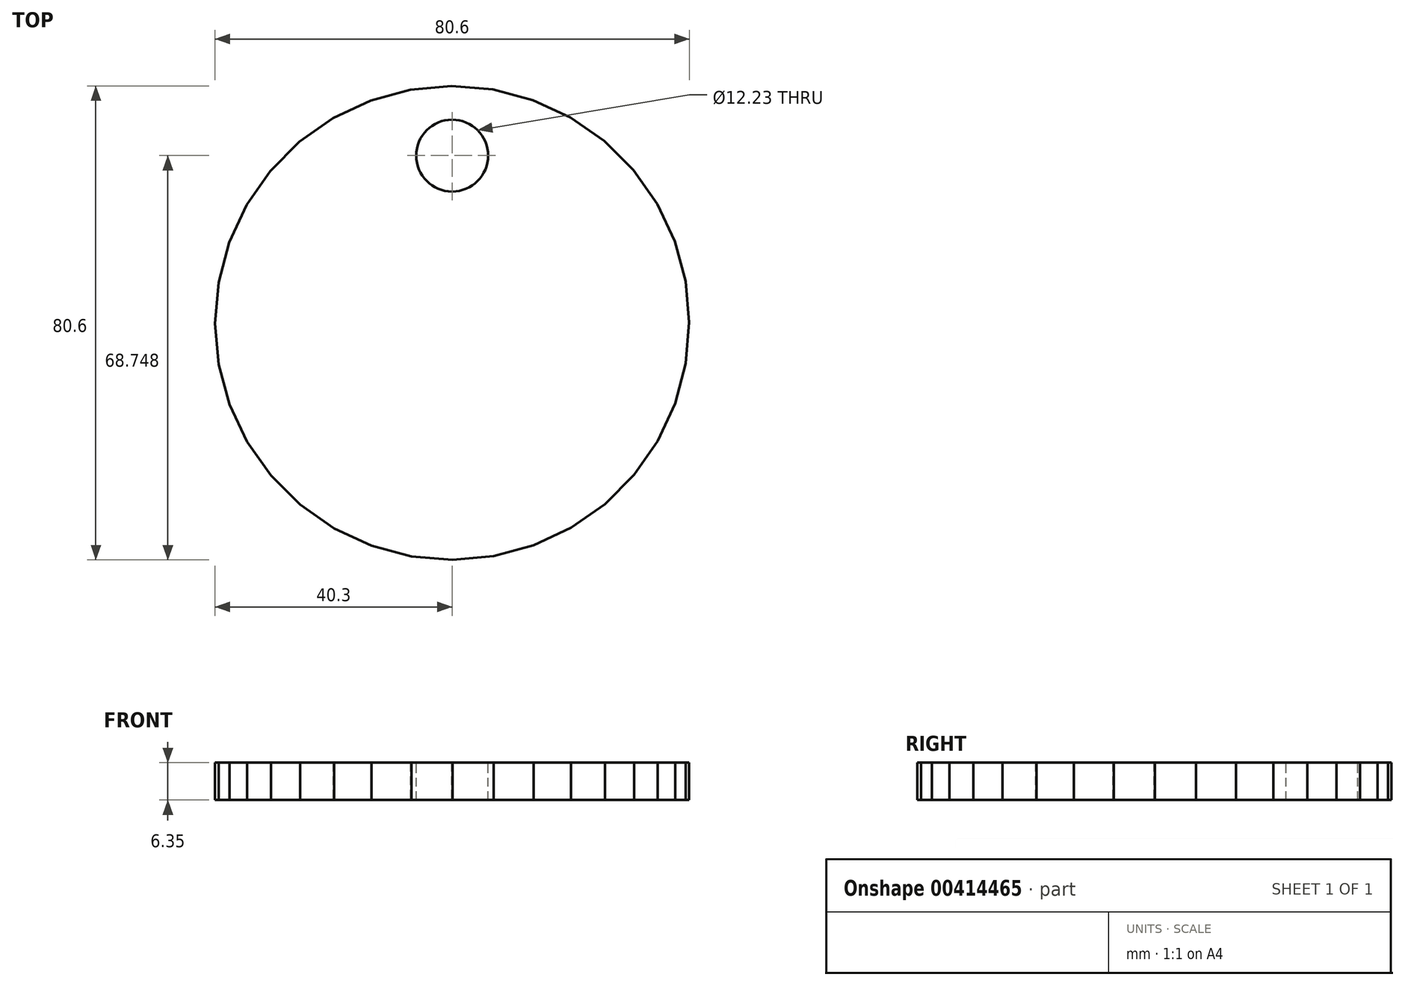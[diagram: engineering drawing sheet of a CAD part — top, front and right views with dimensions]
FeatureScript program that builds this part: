
annotation { "Feature Type Name" : "Feature", "Feature Type Description" : "" }
export const myFeature = defineFeature(function(context is Context, id is Id, definition is map)
    precondition{}
    {
        {
            var Q0;
            Q0=qCreatedBy(makeId("Top.planeOp"),FACE);
            var sketch = newSketch(context, id + "F0", { "sketchPlane" : qUnion([Q0])});
            skCircle(sketch, "E0.cCircle", {"center": v(0, 0) * mm, "radius": 40.3 * mm, "construction": true});
            skLineSegment(sketch, "E0.0", {"start": v(34.85, 20.23) * mm, "end": v(37.84, 13.87) * mm});
            skLineSegment(sketch, "E0.1", {"start": v(37.84, 13.87) * mm, "end": v(39.67, 7.08) * mm});
            skLineSegment(sketch, "E0.2", {"start": v(39.67, 7.08) * mm, "end": v(40.3, 0.09) * mm});
            skLineSegment(sketch, "E0.3", {"start": v(40.3, 0.09) * mm, "end": v(39.7, -6.9) * mm});
            skLineSegment(sketch, "E0.4", {"start": v(39.7, -6.9) * mm, "end": v(37.9, -13.7) * mm});
            skLineSegment(sketch, "E0.5", {"start": v(37.9, -13.7) * mm, "end": v(34.94, -20.07) * mm});
            skLineSegment(sketch, "E0.6", {"start": v(34.94, -20.07) * mm, "end": v(30.93, -25.83) * mm});
            skLineSegment(sketch, "E0.7", {"start": v(30.93, -25.83) * mm, "end": v(25.97, -30.81) * mm});
            skLineSegment(sketch, "E0.8", {"start": v(25.97, -30.81) * mm, "end": v(20.23, -34.85) * mm});
            skLineSegment(sketch, "E0.9", {"start": v(20.23, -34.85) * mm, "end": v(13.87, -37.84) * mm});
            skLineSegment(sketch, "E0.10", {"start": v(13.87, -37.84) * mm, "end": v(7.08, -39.67) * mm});
            skLineSegment(sketch, "E0.11", {"start": v(7.08, -39.67) * mm, "end": v(0.09, -40.3) * mm});
            skLineSegment(sketch, "E0.12", {"start": v(0.09, -40.3) * mm, "end": v(-6.9, -39.7) * mm});
            skLineSegment(sketch, "E0.13", {"start": v(-6.9, -39.7) * mm, "end": v(-13.7, -37.9) * mm});
            skLineSegment(sketch, "E0.14", {"start": v(-13.7, -37.9) * mm, "end": v(-20.07, -34.94) * mm});
            skLineSegment(sketch, "E0.15", {"start": v(-20.07, -34.94) * mm, "end": v(-25.83, -30.93) * mm});
            skLineSegment(sketch, "E0.16", {"start": v(-25.83, -30.93) * mm, "end": v(-30.81, -25.97) * mm});
            skLineSegment(sketch, "E0.17", {"start": v(-30.81, -25.97) * mm, "end": v(-34.85, -20.23) * mm});
            skLineSegment(sketch, "E0.18", {"start": v(-34.85, -20.23) * mm, "end": v(-37.84, -13.87) * mm});
            skLineSegment(sketch, "E0.19", {"start": v(-37.84, -13.87) * mm, "end": v(-39.67, -7.08) * mm});
            skLineSegment(sketch, "E0.20", {"start": v(-39.67, -7.08) * mm, "end": v(-40.3, -0.09) * mm});
            skLineSegment(sketch, "E0.21", {"start": v(-40.3, -0.09) * mm, "end": v(-39.7, 6.9) * mm});
            skLineSegment(sketch, "E0.22", {"start": v(-39.7, 6.9) * mm, "end": v(-37.9, 13.7) * mm});
            skLineSegment(sketch, "E0.23", {"start": v(-37.9, 13.7) * mm, "end": v(-34.94, 20.07) * mm});
            skLineSegment(sketch, "E0.24", {"start": v(-34.94, 20.07) * mm, "end": v(-30.93, 25.83) * mm});
            skLineSegment(sketch, "E0.25", {"start": v(-30.93, 25.83) * mm, "end": v(-25.97, 30.81) * mm});
            skLineSegment(sketch, "E0.26", {"start": v(-25.97, 30.81) * mm, "end": v(-20.23, 34.85) * mm});
            skLineSegment(sketch, "E0.27", {"start": v(-20.23, 34.85) * mm, "end": v(-13.87, 37.84) * mm});
            skLineSegment(sketch, "E0.28", {"start": v(-13.87, 37.84) * mm, "end": v(-7.08, 39.67) * mm});
            skLineSegment(sketch, "E0.29", {"start": v(-7.08, 39.67) * mm, "end": v(-0.09, 40.3) * mm});
            skLineSegment(sketch, "E0.30", {"start": v(-0.09, 40.3) * mm, "end": v(6.9, 39.7) * mm});
            skLineSegment(sketch, "E0.31", {"start": v(6.9, 39.7) * mm, "end": v(13.7, 37.9) * mm});
            skLineSegment(sketch, "E0.32", {"start": v(13.7, 37.9) * mm, "end": v(20.07, 34.94) * mm});
            skLineSegment(sketch, "E0.33", {"start": v(20.07, 34.94) * mm, "end": v(25.83, 30.93) * mm});
            skLineSegment(sketch, "E0.34", {"start": v(25.83, 30.93) * mm, "end": v(30.81, 25.97) * mm});
            skLineSegment(sketch, "E0.35", {"start": v(30.81, 25.97) * mm, "end": v(34.85, 20.23) * mm});
            skSolve(sketch);
        }
        {
            var Q0;
            Q0=makeQuery(id+"F0.imprint","IMPRINT",FACE,{"disambiguationData":[TD([[makeQuery(id+"F0.imprint","IMPRINT",EDGE,{"derivedFrom":sQuery(id+"F0.wireOp",EDGE,"E0.0")}),-1.0]])]});
            extrude(context, id + "F1", {"entities" : qUnion([Q0]), "depth" : 6.35 * mm});
        }
        {
            var Q0;
            Q0=makeQuery(id+"F1.opExtrude","CAP_FACE",FACE,{"disambiguationData":[OSD([sQuery(id+"F0.wireOp",EDGE,"E0.0"),sQuery(id+"F0.wireOp",EDGE,"E0.1"),sQuery(id+"F0.wireOp",EDGE,"E0.2"),sQuery(id+"F0.wireOp",EDGE,"E0.3"),sQuery(id+"F0.wireOp",EDGE,"E0.4"),sQuery(id+"F0.wireOp",EDGE,"E0.5"),sQuery(id+"F0.wireOp",EDGE,"E0.6"),sQuery(id+"F0.wireOp",EDGE,"E0.7"),sQuery(id+"F0.wireOp",EDGE,"E0.8"),sQuery(id+"F0.wireOp",EDGE,"E0.9"),sQuery(id+"F0.wireOp",EDGE,"E0.10"),sQuery(id+"F0.wireOp",EDGE,"E0.11"),sQuery(id+"F0.wireOp",EDGE,"E0.12"),sQuery(id+"F0.wireOp",EDGE,"E0.13"),sQuery(id+"F0.wireOp",EDGE,"E0.14"),sQuery(id+"F0.wireOp",EDGE,"E0.15"),sQuery(id+"F0.wireOp",EDGE,"E0.16"),sQuery(id+"F0.wireOp",EDGE,"E0.17"),sQuery(id+"F0.wireOp",EDGE,"E0.18"),sQuery(id+"F0.wireOp",EDGE,"E0.19"),sQuery(id+"F0.wireOp",EDGE,"E0.20"),sQuery(id+"F0.wireOp",EDGE,"E0.21"),sQuery(id+"F0.wireOp",EDGE,"E0.22"),sQuery(id+"F0.wireOp",EDGE,"E0.23"),sQuery(id+"F0.wireOp",EDGE,"E0.24"),sQuery(id+"F0.wireOp",EDGE,"E0.25"),sQuery(id+"F0.wireOp",EDGE,"E0.26"),sQuery(id+"F0.wireOp",EDGE,"E0.27"),sQuery(id+"F0.wireOp",EDGE,"E0.28"),sQuery(id+"F0.wireOp",EDGE,"E0.29"),sQuery(id+"F0.wireOp",EDGE,"E0.30"),sQuery(id+"F0.wireOp",EDGE,"E0.31"),sQuery(id+"F0.wireOp",EDGE,"E0.32"),sQuery(id+"F0.wireOp",EDGE,"E0.33"),sQuery(id+"F0.wireOp",EDGE,"E0.34"),sQuery(id+"F0.wireOp",EDGE,"E0.35")])],"isStart":false});
            var sketch = newSketch(context, id + "F2", { "sketchPlane" : qUnion([Q0])});
            skText(sketch, "E1", { "text": "2017!", "fontName": "OpenSans-Bold.ttf"});
            const initialGuessF2  = {"E1": [-0.0351, -0.00954, 1, 0, 0.01984]};
            skSetInitialGuess(sketch, initialGuessF2);
            skSolve(sketch);
        }
        {
            var Q0;
            Q0 = qConstructionFilter(qBodyType(qCreatedBy(id + "F2" ,EDGE), BodyType.WIRE), ConstructionObject.NO);
            extrude(context, id + "F3", {"bodyType" : ToolBodyType.SURFACE, "surfaceEntities" : qUnion([Q0]), "depth" : 2.54 * mm});
        }
        {
            var Q0;
            Q0=makeQuery(id+"F1.opExtrude","CAP_FACE",FACE,{"disambiguationData":[OSD([sQuery(id+"F0.wireOp",EDGE,"E0.0"),sQuery(id+"F0.wireOp",EDGE,"E0.1"),sQuery(id+"F0.wireOp",EDGE,"E0.2"),sQuery(id+"F0.wireOp",EDGE,"E0.3"),sQuery(id+"F0.wireOp",EDGE,"E0.4"),sQuery(id+"F0.wireOp",EDGE,"E0.5"),sQuery(id+"F0.wireOp",EDGE,"E0.6"),sQuery(id+"F0.wireOp",EDGE,"E0.7"),sQuery(id+"F0.wireOp",EDGE,"E0.8"),sQuery(id+"F0.wireOp",EDGE,"E0.9"),sQuery(id+"F0.wireOp",EDGE,"E0.10"),sQuery(id+"F0.wireOp",EDGE,"E0.11"),sQuery(id+"F0.wireOp",EDGE,"E0.12"),sQuery(id+"F0.wireOp",EDGE,"E0.13"),sQuery(id+"F0.wireOp",EDGE,"E0.14"),sQuery(id+"F0.wireOp",EDGE,"E0.15"),sQuery(id+"F0.wireOp",EDGE,"E0.16"),sQuery(id+"F0.wireOp",EDGE,"E0.17"),sQuery(id+"F0.wireOp",EDGE,"E0.18"),sQuery(id+"F0.wireOp",EDGE,"E0.19"),sQuery(id+"F0.wireOp",EDGE,"E0.20"),sQuery(id+"F0.wireOp",EDGE,"E0.21"),sQuery(id+"F0.wireOp",EDGE,"E0.22"),sQuery(id+"F0.wireOp",EDGE,"E0.23"),sQuery(id+"F0.wireOp",EDGE,"E0.24"),sQuery(id+"F0.wireOp",EDGE,"E0.25"),sQuery(id+"F0.wireOp",EDGE,"E0.26"),sQuery(id+"F0.wireOp",EDGE,"E0.27"),sQuery(id+"F0.wireOp",EDGE,"E0.28"),sQuery(id+"F0.wireOp",EDGE,"E0.29"),sQuery(id+"F0.wireOp",EDGE,"E0.30"),sQuery(id+"F0.wireOp",EDGE,"E0.31"),sQuery(id+"F0.wireOp",EDGE,"E0.32"),sQuery(id+"F0.wireOp",EDGE,"E0.33"),sQuery(id+"F0.wireOp",EDGE,"E0.34"),sQuery(id+"F0.wireOp",EDGE,"E0.35")])],"isStart":false});
            var sketch = newSketch(context, id + "F4", { "sketchPlane" : qUnion([Q0])});
            skCircle(sketch, "E2", {"center": v(0, 28.45) * mm, "radius": 6.11 * mm});
            skPoint(sketch, "E2.centerSnap0", {"position": v(28.32, 28.45) * mm});
            skSolve(sketch);
        }
        {
            var Q0;
            Q0=makeQuery(id+"F4.imprint","IMPRINT",FACE,{"disambiguationData":[TD([[makeQuery(id+"F4.imprint","IMPRINT",EDGE,{"derivedFrom":sQuery(id+"F4.wireOp",EDGE,"E2")}),1.0]])]});
            extrude(context, id + "F5", {"entities" : qUnion([Q0]), "operationType" : NewBodyOperationType.REMOVE, "endBound" : BoundingType.THROUGH_ALL, "oppositeDirection" : true, "depth" : -20.32 * mm});
        }
    });
